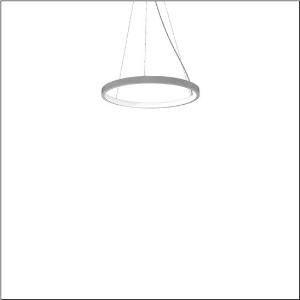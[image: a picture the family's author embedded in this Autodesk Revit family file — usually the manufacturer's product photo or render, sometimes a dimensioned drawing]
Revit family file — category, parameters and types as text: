
# Revit family: silica_r__21_ring-i_5pjbi1d1204a_31f3
name_source: partatom
category: Lighting Fixtures
units: mm (PartAtom-declared; Revit-internal decimal feet)

## family parameters
Cut with Voids When Loaded = No
Host = Face
Light Source = No
Part Type = Normal
Room Calculation Point = No
Round Connector Dimension = Use Diameter
Shared = No

## types (1)
- Silica® 21 Ring-I (1 x LED, 3430 lm, 60 W, 3000K)
    Apparent Load = 60 VA
    CIE Flux Codes = 22 48 76 50 101
    Color Rendering = 80
    Color Temperature = 3000K
    Default Elevation = 1800 mm
    Description = Silica® 21 Ring-I, suspended luminaire, of PMMA, frosted, light emission: inner ring side luminous distribution, primary light characteristic: symmetric, installation type: suspended mounting, LED, rated luminous flux: 3.430lm, luminous efficacy: 57lm/W, light colour: 830, colour temperature: 3000K, with terminal, 5-pole, mains connection: 230V, AC/DC, 0/50..60Hz, rated input power: 60W, housing, of extruded aluminium section, metallic grey (RAL 9006), diameter: 610mm, ceiling canopy, metallic grey (RAL 9006), protection rating (lamp compartment): IP40, insulation class (complete): insulation class I (protective earthing), certification: CE, impact resistance: IK02, permissible operating ambient temperature: 0..+35°C, packaging unit: 1 piece
    Height = 48 mm  [stored 0.15748 ft]
    Lamp = 1 x LED
    Lamp Light Flux = 3430 lm
    Lamp Power = 60 W
    Lamp count = 1
    Length = 610 mm
    Luminous efficacy = 57 lm/W
    Manufacturer = Siteco
    ModVariant = No
    Model = 5PJBI1D1204A
    Mounting Place = Ceiling
    Mounting Type = Pendant
    Number of Poles = 1
    OnlyDefault = Yes
    Power Factor = 1
    Product Name = Silica® 21 Ring-I
    Product group = suspended luminaire
    ProductGroupID = 904
    Protection Class = Protection class I
    Protection Degree = IP 40
    RLX_Detail_Level = 1
    RLX_Emergency_Light_Flux = 0 lm
    RLX_Emergency_Type = 0
    RLX_Emergency_Type_DB = No
    RlxData = <blob elided: 11489 chars, md5=38638b63>
    Socket = socket
    Standby Power = 0 W
    System Light Flux = 3430 lm
    System Power = 60 W
    Type Comments = Product without accessories
    Type Image = l_1251750.jpg
    URL = http://relux.com
    VarID = ---
    Voltage = 0 V
    Weight = 0.00 kg
    Width = 0 mm  [stored 0 ft]

note: [stored X ft] marks values corroborated as IEEE doubles in the binary element streams (Revit-internal decimal feet)

## geometry (parser evidence)
native form markers: Sweep x11
no freeform markers — native parametric forms only
